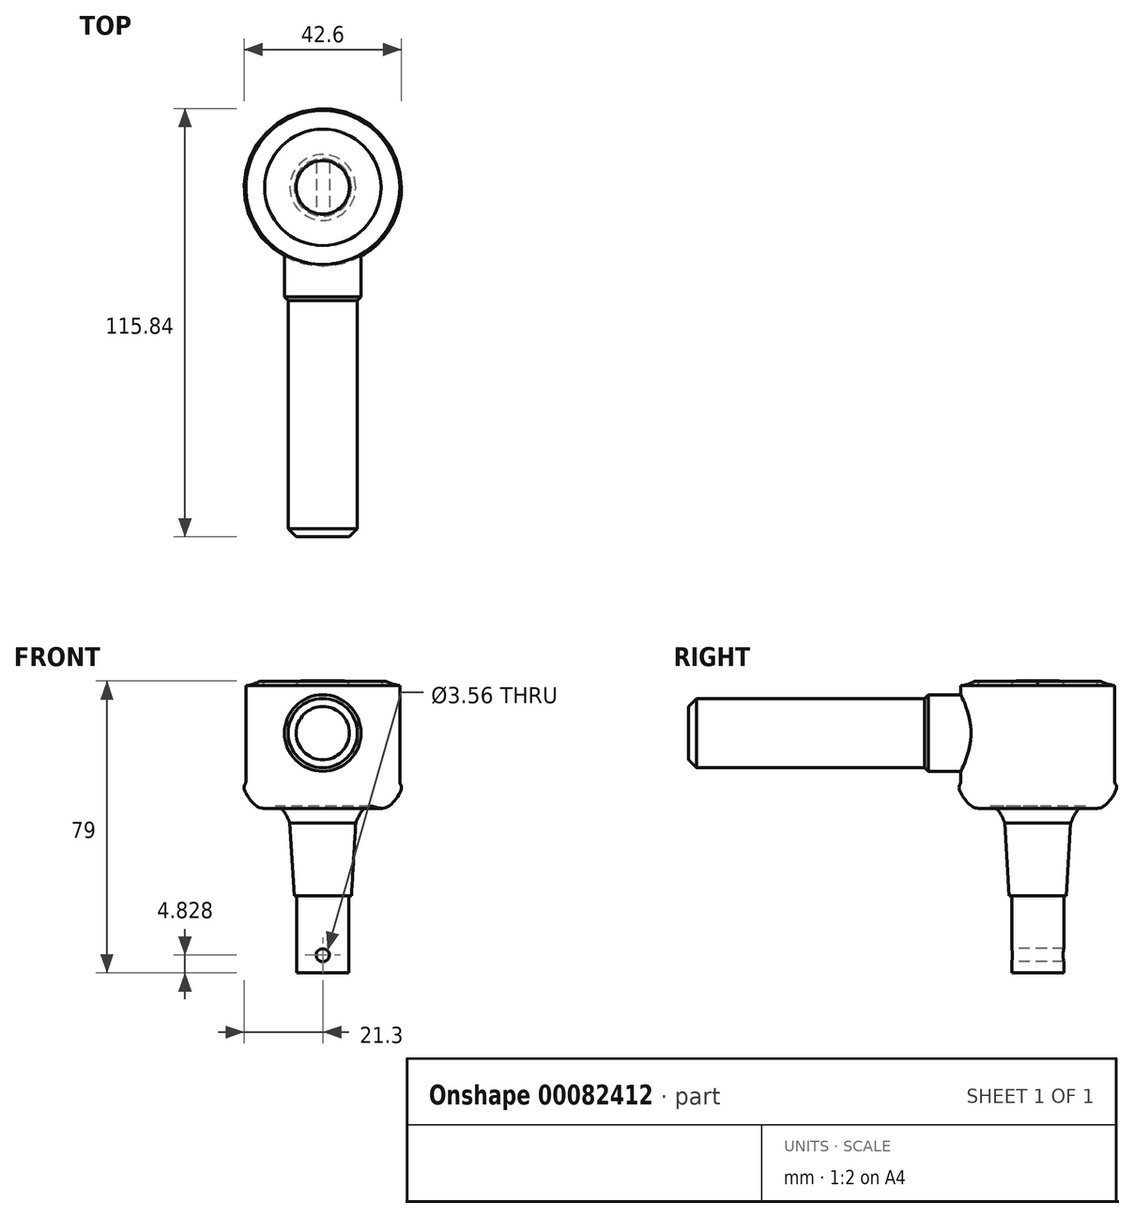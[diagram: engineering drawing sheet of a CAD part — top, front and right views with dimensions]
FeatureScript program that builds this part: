
annotation { "Feature Type Name" : "Feature", "Feature Type Description" : "" }
export const myFeature = defineFeature(function(context is Context, id is Id, definition is map)
    precondition{}
    {
        {
            var Q0;
            Q0=qCreatedBy(makeId("Front.planeOp"),FACE);
            var sketch = newSketch(context, id + "F0", { "sketchPlane" : qUnion([Q0])});
            skLineSegment(sketch, "E0", {"start": v(0, 58.17) * mm, "end": v(0, -75.16) * mm});
            skLineSegment(sketch, "E1.top", {"start": v(0, -20.83) * mm, "end": v(7.06, -20.83) * mm});
            skLineSegment(sketch, "E1.left", {"start": v(0, 0) * mm, "end": v(0, -20.83) * mm});
            skLineSegment(sketch, "E1.right", {"start": v(7.06, 0) * mm, "end": v(7.06, -20.83) * mm});
            skLineSegment(sketch, "E2.bottom", {"start": v(7.06, 0) * mm, "end": v(7.75, 0) * mm});
            skLineSegment(sketch, "E2.left", {"start": v(0, 0) * mm, "end": v(0, 19.68) * mm});
            skLineSegment(sketch, "E3.left", {"start": v(0, 19.68) * mm, "end": v(0, 30.23) * mm});
            skLineSegment(sketch, "E4.top", {"start": v(0, 58.17) * mm, "end": v(6.35, 58.17) * mm});
            skLineSegment(sketch, "E4.right", {"start": v(20.83, 30.23) * mm, "end": v(20.83, 56.9) * mm});
            skPoint(sketch, "E5.orphan", {"position": v(0, 75.3) * mm});
            skPoint(sketch, "E2.top.end.orphan", {"position": v(7.75, 19.68) * mm});
            skLineSegment(sketch, "E6", {"start": v(7.75, 0) * mm, "end": v(8.9, 19.69) * mm});
            skFitSpline(sketch, "E7", {"points": [v(8.9, 19.68) * mm, v(16.92, 23.85) * mm, v(20.83, 30.23) * mm], "startDerivative": vector(16.51, 43.56) * mm, "endDerivative": vector(-10.4, 2.48) * mm});
            skPoint(sketch, "E4.bottom.start.orphan", {"position": v(8.9, 30.23) * mm});
            skLineSegment(sketch, "E8.0", {"start": v(7.24, 56.9) * mm, "end": v(15.75, 56.9) * mm});
            skFitSpline(sketch, "E9", {"points": [v(15.75, 56.9) * mm, v(20.83, 56.9) * mm], "startDerivative": vector(3.74, 7.1) * mm, "endDerivative": vector(13.64, -2.25) * mm});
            skPoint(sketch, "E10.orphan", {"position": v(20.83, 58.17) * mm});
            skPoint(sketch, "E11.orphan", {"position": v(15.75, 58.17) * mm});
            skLineSegment(sketch, "E12.0", {"start": v(7.24, 56.9) * mm, "end": v(7.24, 58.17) * mm});
            skLineSegment(sketch, "E13", {"start": v(6.35, 58.17) * mm, "end": v(7.24, 58.17) * mm});
            skSolve(sketch);
        }
        {
            var Q0;
            Q0=makeQuery(id+"F0.imprint","IMPRINT",FACE,{"disambiguationData":[TD([[makeQuery(id+"F0.imprint","IMPRINT",EDGE,{"derivedFrom":sQuery(id+"F0.wireOp",EDGE,"E1.top")}),1.0]])]});
            var Q1;
            Q1=sQuery(id+"F0.wireOp",EDGE,"E0");
            revolve(context, id + "F1", {"entities" : qUnion([Q0]), "axis" : qUnion([Q1]), "revolveType" : RevolveType.FULL});
        }
        {
            var Q0;
            Q0=qCreatedBy(makeId("Front.planeOp"),FACE);
            var sketch = newSketch(context, id + "F2", { "sketchPlane" : qUnion([Q0])});
            skCircle(sketch, "E14", {"center": v(0, -16) * mm, "radius": 1.78 * mm});
            skPoint(sketch, "E15.center.orphan", {"position": v(0, -20.83) * mm});
            skSolve(sketch);
        }
        {
            var Q0;
            Q0 = qSketchRegion(id + "F2", true);
            extrude(context, id + "F3", {"entities" : qUnion([Q0]), "operationType" : NewBodyOperationType.REMOVE, "endBound" : BoundingType.SYMMETRIC, "oppositeDirection" : true, "depth" : 25.4 * mm});
        }
        {
            var Q0;
            Q0=qCreatedBy(makeId("Front.planeOp"),FACE);
            var sketch = newSketch(context, id + "F4", { "sketchPlane" : qUnion([Q0])});
            skLineSegment(sketch, "E16", {"start": v(0, 0) * mm, "end": v(0, 44.07) * mm});
            skCircle(sketch, "E17", {"center": v(0, 44.07) * mm, "radius": 10.35 * mm});
            skSolve(sketch);
        }
        {
            var Q0;
            Q0 = qSketchRegion(id + "F4", true);
            extrude(context, id + "F5", {"entities" : qUnion([Q0]), "operationType" : NewBodyOperationType.ADD, "depth" : 31.75 * mm});
        }
        {
            var Q0;
            Q0=makeQuery(id+"F5.opExtrude","CAP_FACE",FACE,{"disambiguationData":[OSD([sQuery(id+"F4.wireOp",EDGE,"E17")])],"isStart":false});
            var sketch = newSketch(context, id + "F6", { "sketchPlane" : qUnion([Q0])});
            skCircle(sketch, "E18", {"center": v(0, 44.07) * mm, "radius": 9.36 * mm});
            skSolve(sketch);
        }
        {
            var Q0;
            Q0=makeQuery(id+"F6.imprint","IMPRINT",FACE,{"disambiguationData":[TD([[makeQuery(id+"F6.imprint","IMPRINT",EDGE,{"derivedFrom":sQuery(id+"F6.wireOp",EDGE,"E18")}),1.0]])]});
            extrude(context, id + "F7", {"entities" : qUnion([Q0]), "operationType" : NewBodyOperationType.ADD, "depth" : 62.8 * mm});
        }
        {
            var Q0;
            Q0=makeQuery(id+"F5.opExtrude","CAP_EDGE",EDGE,{"disambiguationData":[OSD([sQuery(id+"F4.wireOp",EDGE,"E17")])],"isStart":false});
            var Q1;
            Q1=makeQuery(id+"F7.opExtrude","CAP_EDGE",EDGE,{"disambiguationData":[OSD([sQuery(id+"F6.wireOp",EDGE,"E18")])],"isStart":false});
            chamfer(context, id + "F8", {"entities" : qUnion([Q0, Q1]), "width" : 2.16 * mm, "tangentPropagation" : true});
        }
        {
            var Q0;
            Q0=makeQuery(id+"F1.opRevolve","SWEPT_EDGE",EDGE,{"disambiguationData":[OSD([sQuery(id+"F0.wireOp",EDGE,"E12.0"),sQuery(id+"F0.wireOp",EDGE,"E13")])]});
            var Q1;
            Q1=makeQuery(id+"F1.opRevolve","SWEPT_EDGE",EDGE,{"disambiguationData":[OSD([sQuery(id+"F0.wireOp",EDGE,"E4.right"),sQuery(id+"F0.wireOp",EDGE,"E7")])]});
            fillet(context, id + "F9", {"entities" : qUnion([Q0, Q1]), "radius" : 1.65 * mm, "tangentPropagation" : true, "allowEdgeOverflow" : false});
        }
    });
